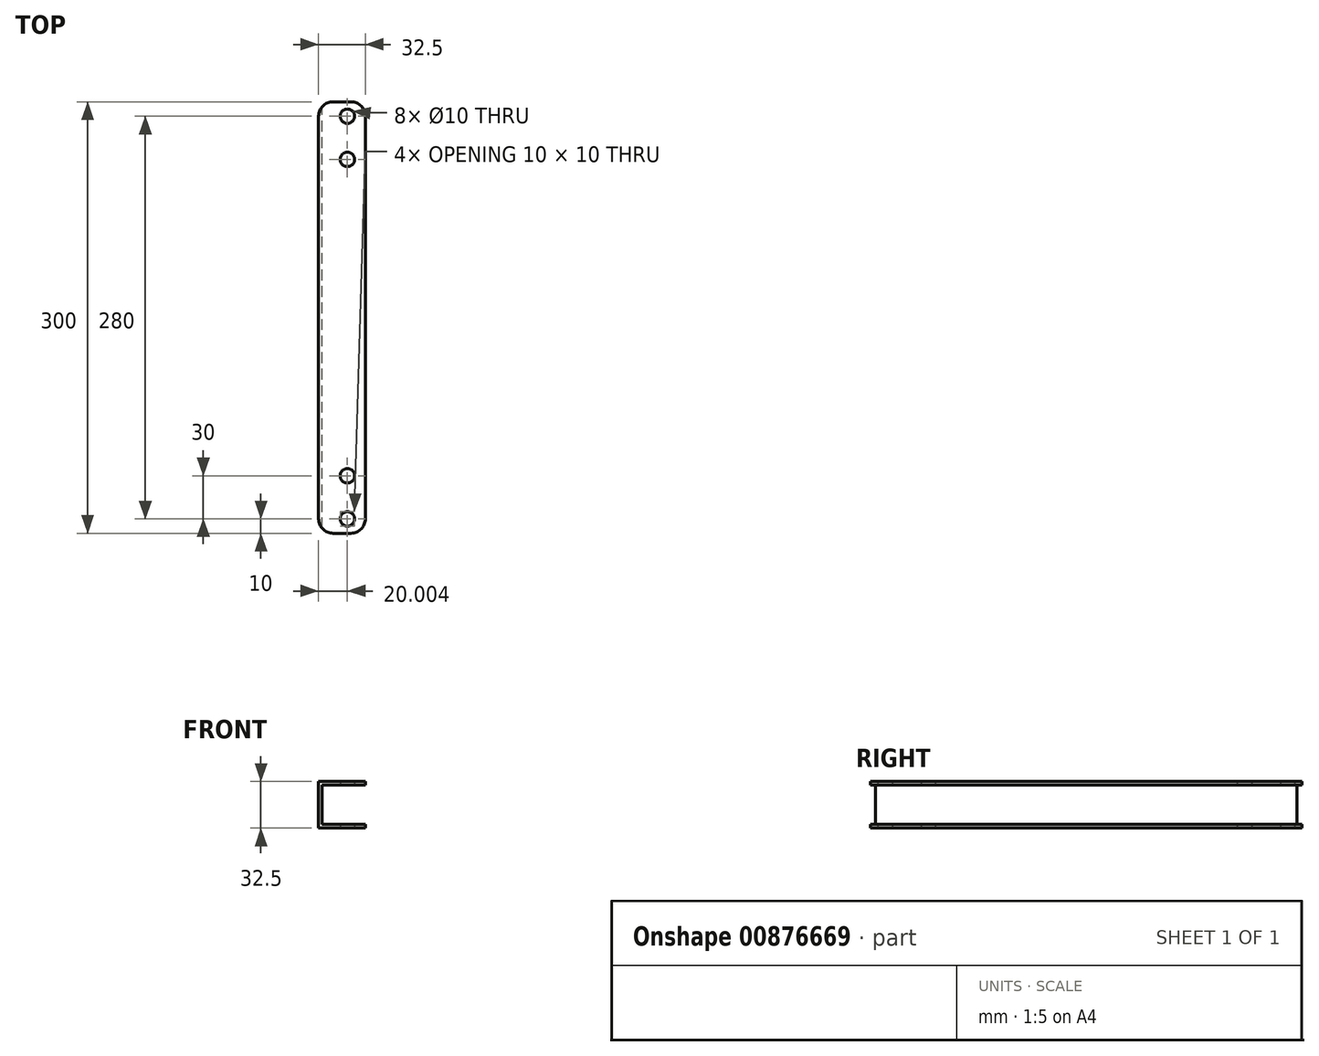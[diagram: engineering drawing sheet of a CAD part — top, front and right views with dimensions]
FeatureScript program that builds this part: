
annotation { "Feature Type Name" : "Feature", "Feature Type Description" : "" }
export const myFeature = defineFeature(function(context is Context, id is Id, definition is map)
    precondition{}
    {
        {
            var Q0;
            Q0=qCreatedBy(makeId("Front.planeOp"),FACE);
            var sketch = newSketch(context, id + "F0", { "sketchPlane" : qUnion([Q0])});
            skLineSegment(sketch, "E0.bottom", {"start": v(-74.99, 0) * mm, "end": v(-42.49, 0) * mm});
            skLineSegment(sketch, "E0.top", {"start": v(-74.99, 32.5) * mm, "end": v(-42.49, 32.5) * mm});
            skLineSegment(sketch, "E0.left", {"start": v(-74.99, 0) * mm, "end": v(-74.99, 32.5) * mm});
            skLineSegment(sketch, "E0.right", {"start": v(-42.49, 0) * mm, "end": v(-42.49, 2.5) * mm});
            skLineSegment(sketch, "E1.top", {"start": v(-42.49, 2.5) * mm, "end": v(-72.49, 2.5) * mm});
            skLineSegment(sketch, "E2.top", {"start": v(-42.49, 30) * mm, "end": v(-72.49, 30) * mm});
            skLineSegment(sketch, "E3.trimOffspring", {"start": v(-42.49, 30) * mm, "end": v(-42.49, 32.5) * mm});
            skPoint(sketch, "E2.left.start.orphan", {"position": v(-42.49, 16.25) * mm});
            skLineSegment(sketch, "E4", {"start": v(-72.49, 30) * mm, "end": v(-72.49, 2.5) * mm});
            skSolve(sketch);
        }
        {
            var Q0;
            Q0=qCreatedBy(makeId("Top.planeOp"),FACE);
            var sketch = newSketch(context, id + "F1", { "sketchPlane" : qUnion([Q0])});
            skLineSegment(sketch, "E5.0", {"start": v(0, -150) * mm, "end": v(-82.52, -150) * mm, "construction": true});
            skLineSegment(sketch, "E6.bottom", {"start": v(-59.99, -290) * mm, "end": v(-54.99, -290) * mm});
            skCircle(sketch, "E7", {"center": v(-54.99, -10) * mm, "radius": 5 * mm});
            skCircle(sketch, "E8", {"center": v(-54.99, -290) * mm, "radius": 5 * mm});
            skCircle(sketch, "E9", {"center": v(-54.99, -260) * mm, "radius": 5 * mm});
            skCircle(sketch, "E10", {"center": v(-54.99, -40) * mm, "radius": 5 * mm});
            skSolve(sketch);
        }
        {
            var Q0;
            Q0=makeQuery(id+"F0.imprint","IMPRINT",FACE,{"disambiguationData":[TD([[makeQuery(id+"F0.imprint","IMPRINT",EDGE,{"derivedFrom":sQuery(id+"F0.wireOp",EDGE,"E0.bottom")}),1.0]])]});
            extrude(context, id + "F2", {"entities" : qUnion([Q0]), "depth" : 300 * mm, "offsetDistance" : 25 * mm});
        }
        {
            var Q0;
            Q0=makeQuery(id+"F1.imprint","IMPRINT",FACE,{"disambiguationData":[TD([[makeQuery(id+"F1.imprint","IMPRINT",EDGE,{"derivedFrom":sQuery(id+"F1.wireOp",EDGE,"E8")}),1.0]])]});
            var Q1;
            Q1=makeQuery(id+"F1.imprint","IMPRINT",FACE,{"disambiguationData":[TD([[makeQuery(id+"F1.imprint","IMPRINT",EDGE,{"derivedFrom":sQuery(id+"F1.wireOp",EDGE,"E9")}),1.0]])]});
            var Q2;
            Q2=makeQuery(id+"F1.imprint","IMPRINT",FACE,{"disambiguationData":[TD([[makeQuery(id+"F1.imprint","IMPRINT",EDGE,{"derivedFrom":sQuery(id+"F1.wireOp",EDGE,"E10")}),1.0]])]});
            var Q3;
            Q3=makeQuery(id+"F1.imprint","IMPRINT",FACE,{"disambiguationData":[TD([[makeQuery(id+"F1.imprint","IMPRINT",EDGE,{"derivedFrom":sQuery(id+"F1.wireOp",EDGE,"E7")}),1.0]])]});
            extrude(context, id + "F3", {"entities" : qUnion([Q0, Q1, Q2, Q3]), "operationType" : NewBodyOperationType.REMOVE, "depth" : 46 * mm, "offsetDistance" : 25 * mm});
        }
        {
            var Q0;
            Q0=makeQuery(id+"F2.opExtrude","CAP_EDGE",EDGE,{"disambiguationData":[OSD([sQuery(id+"F0.wireOp",EDGE,"E0.right")])],"isStart":true});
            var Q1;
            Q1=makeQuery(id+"F2.opExtrude","CAP_EDGE",EDGE,{"disambiguationData":[OSD([sQuery(id+"F0.wireOp",EDGE,"E3.trimOffspring")])],"isStart":true});
            var Q2;
            Q2=makeQuery(id+"F2.opExtrude","CAP_EDGE",EDGE,{"disambiguationData":[OSD([sQuery(id+"F0.wireOp",EDGE,"E3.trimOffspring")])],"isStart":false});
            var Q3;
            Q3=makeQuery(id+"F2.opExtrude","CAP_EDGE",EDGE,{"disambiguationData":[OSD([sQuery(id+"F0.wireOp",EDGE,"E0.right")])],"isStart":false});
            var Q4;
            Q4=makeQuery(id+"F2.opExtrude","CAP_EDGE",EDGE,{"disambiguationData":[OSD([sQuery(id+"F0.wireOp",EDGE,"E0.left")])],"isStart":true});
            var Q5;
            Q5=makeQuery(id+"F2.opExtrude","CAP_EDGE",EDGE,{"disambiguationData":[OSD([sQuery(id+"F0.wireOp",EDGE,"E0.left")])],"isStart":false});
            fillet(context, id + "F4", {"entities" : qUnion([Q0, Q1, Q2, Q3, Q4, Q5]), "radius" : 10 * mm, "tangentPropagation" : true, "allowEdgeOverflow" : false});
        }
    });
